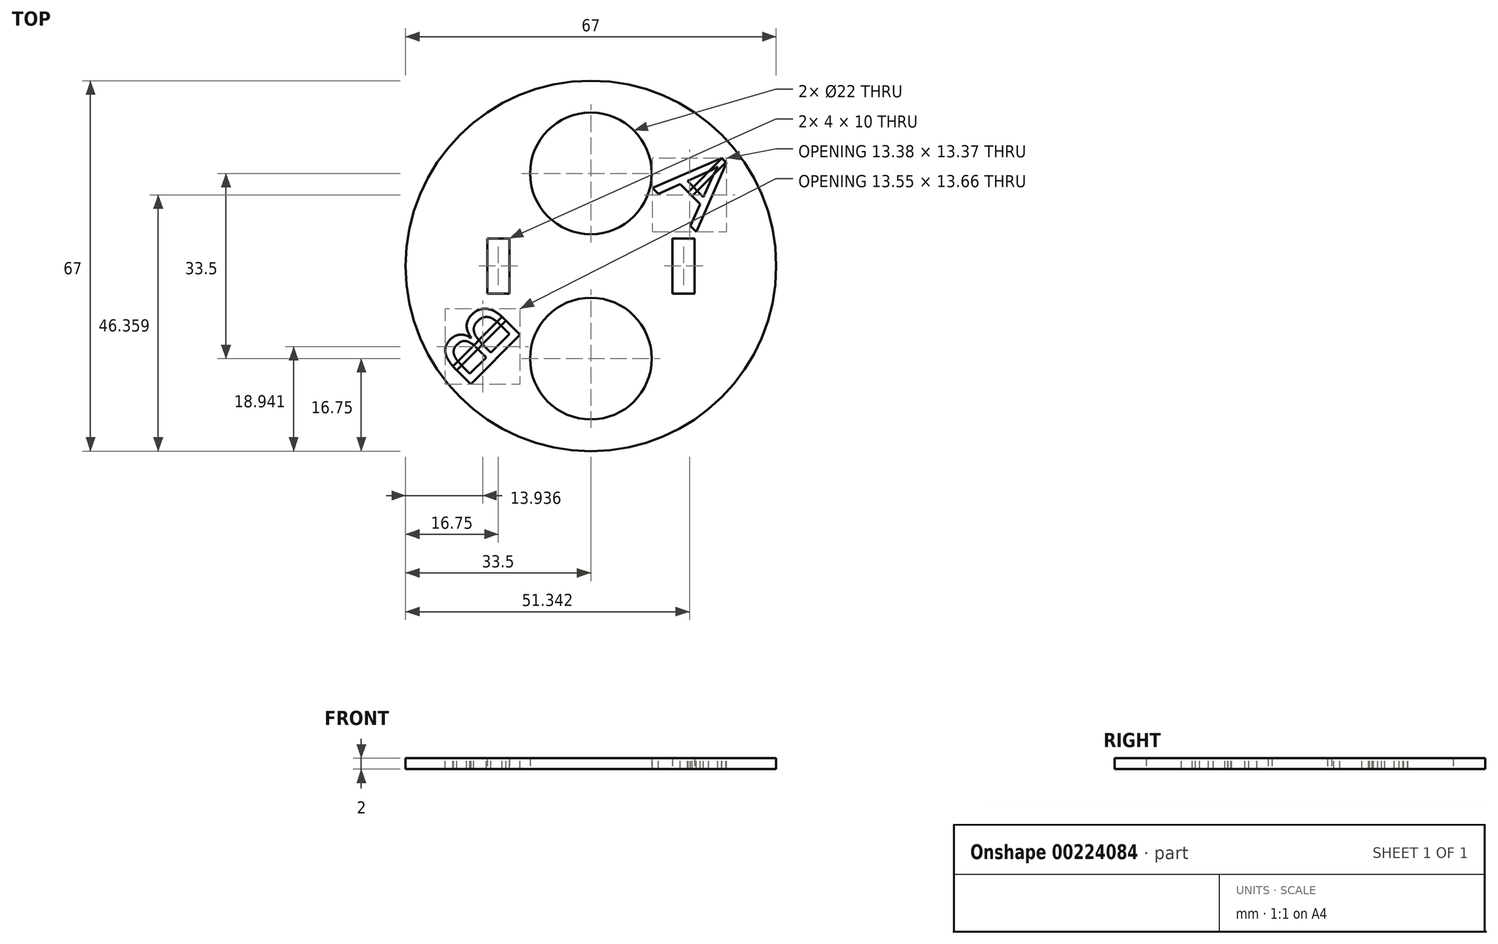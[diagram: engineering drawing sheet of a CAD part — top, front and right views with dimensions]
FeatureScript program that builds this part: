
annotation { "Feature Type Name" : "Feature", "Feature Type Description" : "" }
export const myFeature = defineFeature(function(context is Context, id is Id, definition is map)
    precondition{}
    {
        {
            assignVariable(context, id + "F0", {"name" : "thickness", "anyValue" : 2});
        }
        {
            var Q0;
            Q0=qCreatedBy(makeId("Top.planeOp"),FACE);
            var sketch = newSketch(context, id + "F1", { "sketchPlane" : qUnion([Q0])});
            skCircle(sketch, "E0", {"center": v(0, 0) * mm, "radius": 33.5 * mm});
            skLineSegment(sketch, "E1", {"start": v(0, 41.8) * mm, "end": v(0, -44.03) * mm});
            skLineSegment(sketch, "E2", {"start": v(41.2, 0) * mm, "end": v(-39.2, 0) * mm});
            skLineSegment(sketch, "E3", {"start": v(0, 0) * mm, "end": v(0, 33.5) * mm});
            skLineSegment(sketch, "E4", {"start": v(0, 33.5) * mm, "end": v(0, 16.75) * mm});
            skLineSegment(sketch, "E5", {"start": v(0, 0) * mm, "end": v(0, -16.75) * mm});
            skLineSegment(sketch, "E6", {"start": v(0, 0) * mm, "end": v(-16.75, 0) * mm});
            skLineSegment(sketch, "E7", {"start": v(0, 0) * mm, "end": v(16.75, 0) * mm});
            skCircle(sketch, "E8", {"center": v(0, 16.75) * mm, "radius": 11 * mm});
            skCircle(sketch, "E9", {"center": v(0, -16.75) * mm, "radius": 11 * mm});
            skLineSegment(sketch, "E10.bottom", {"start": v(-18.75, 5) * mm, "end": v(-14.75, 5) * mm});
            skLineSegment(sketch, "E10.top", {"start": v(-18.75, -5) * mm, "end": v(-14.75, -5) * mm});
            skLineSegment(sketch, "E10.left", {"start": v(-18.75, 5) * mm, "end": v(-18.75, -5) * mm});
            skLineSegment(sketch, "E10.right", {"start": v(-14.75, 5) * mm, "end": v(-14.75, -5) * mm});
            skPoint(sketch, "E10.middle", {"position": v(-16.75, 0) * mm});
            skLineSegment(sketch, "E11.bottom", {"start": v(14.75, 5) * mm, "end": v(18.75, 5) * mm});
            skLineSegment(sketch, "E11.top", {"start": v(14.75, -5) * mm, "end": v(18.75, -5) * mm});
            skLineSegment(sketch, "E11.left", {"start": v(14.75, 5) * mm, "end": v(14.75, -5) * mm});
            skLineSegment(sketch, "E11.right", {"start": v(18.75, 5) * mm, "end": v(18.75, -5) * mm});
            skPoint(sketch, "E11.middle", {"position": v(16.75, 0) * mm});
            skSolve(sketch);
        }
        {
            var Q0;
            {var subQ6=sQuery(id+"F1.wireOp",EDGE,"E2");var subQ9=sQuery(id+"F1.wireOp",EDGE,"E0");var subQ10=makeQuery(id+"F1.imprint","INTERSECT",VERTEX,{"disambiguationData":[OD(1.0)],"derivedFrom":[subQ9,subQ6]});Q0=makeQuery(id+"F1.imprint","IMPRINT",FACE,{"disambiguationData":[TD([[makeQuery(id+"F1.imprint","IMPRINT",EDGE,{"disambiguationData":[TD([[subQ10,-1.0]])],"derivedFrom":subQ9}),1.0]])]});}
            var Q1;
            {var subQ0=sQuery(id+"F1.wireOp",EDGE,"E4");var subQ1=sQuery(id+"F1.wireOp",EDGE,"E0");var subQ2=makeQuery(id+"F1.imprint","INTERSECT",VERTEX,{"derivedFrom":[subQ1,subQ0]});Q1=makeQuery(id+"F1.imprint","IMPRINT",FACE,{"disambiguationData":[TD([[makeQuery(id+"F1.imprint","IMPRINT",EDGE,{"disambiguationData":[TD([[subQ2,-1.0]])],"derivedFrom":subQ1}),1.0]])]});}
            var Q2;
            {var subQ0=sQuery(id+"F1.wireOp",EDGE,"E4");var subQ1=sQuery(id+"F1.wireOp",EDGE,"E0");var subQ2=makeQuery(id+"F1.imprint","INTERSECT",VERTEX,{"derivedFrom":[subQ1,subQ0]});Q2=makeQuery(id+"F1.imprint","IMPRINT",FACE,{"disambiguationData":[TD([[makeQuery(id+"F1.imprint","IMPRINT",EDGE,{"disambiguationData":[TD([[subQ2,1.0]])],"derivedFrom":subQ1}),1.0]])]});}
            var Q3;
            {var subQ5=sQuery(id+"F1.wireOp",EDGE,"E2");var subQ6=sQuery(id+"F1.wireOp",EDGE,"E0");var subQ7=makeQuery(id+"F1.imprint","INTERSECT",VERTEX,{"disambiguationData":[OD(0.0)],"derivedFrom":[subQ6,subQ5]});Q3=makeQuery(id+"F1.imprint","IMPRINT",FACE,{"disambiguationData":[TD([[makeQuery(id+"F1.imprint","IMPRINT",EDGE,{"disambiguationData":[TD([[subQ7,1.0]])],"derivedFrom":subQ6}),1.0]])]});}
            extrude(context, id + "F2", {"entities" : qUnion([Q0, Q1, Q2, Q3]), "depth" : (getVariable(context, 'thickness')) * mm});
        }
        {
            var Q0;
            Q0=makeQuery(id+"F2.opExtrude","CAP_FACE",FACE,{"disambiguationData":[OSD([sQuery(id+"F1.wireOp",EDGE,"E0"),sQuery(id+"F1.wireOp",EDGE,"E8"),sQuery(id+"F1.wireOp",EDGE,"E9"),sQuery(id+"F1.wireOp",EDGE,"E10.bottom"),sQuery(id+"F1.wireOp",EDGE,"E10.top"),sQuery(id+"F1.wireOp",EDGE,"E10.left"),sQuery(id+"F1.wireOp",EDGE,"E10.right"),sQuery(id+"F1.wireOp",EDGE,"E11.bottom"),sQuery(id+"F1.wireOp",EDGE,"E11.top"),sQuery(id+"F1.wireOp",EDGE,"E11.left"),sQuery(id+"F1.wireOp",EDGE,"E11.right")])],"isStart":false});
            var sketch = newSketch(context, id + "F3", { "sketchPlane" : qUnion([Q0])});
            skText(sketch, "E12", { "text": "A", "fontName": "OpenSans-Regular.ttf"});
            skText(sketch, "E13", { "text": "B", "fontName": "OpenSans-Regular.ttf"});
            skLineSegment(sketch, "E14", {"start": v(23.02, 17.94) * mm, "end": v(22.98, 17.9) * mm});
            skLineSegment(sketch, "E15", {"start": v(23.34, 17.55) * mm, "end": v(17.35, 11.56) * mm});
            const initialGuessF3  = {"E12": [0.01115, 0.0141, 0.7071, -0.7071, 0.01275], "E13": [-0.01156, -0.01368, -0.7071, 0.7071, 0.01275]};
            skSetInitialGuess(sketch, initialGuessF3);
            skSolve(sketch);
        }
        {
            var Q0;
            Q0=makeQuery(id+"F3.imprint","IMPRINT",FACE,{"disambiguationData":[TD([[makeQuery(id+"F3.imprint","IMPRINT",EDGE,{"derivedFrom":sQuery(id+"F3.wireOp",EDGE,"E13.sketch_text.stroke-0")}),-1.0]])]});
            var Q1;
            {var subQ1=sQuery(id+"F3.wireOp",EDGE,"E12.sketch_text.stroke-0");Q1=makeQuery(id+"F3.imprint","IMPRINT",FACE,{"disambiguationData":[TD([[makeQuery(id+"F3.imprint","IMPRINT",EDGE,{"derivedFrom":subQ1}),-1.0]])]});}
            extrude(context, id + "F4", {"entities" : qUnion([Q0, Q1]), "operationType" : NewBodyOperationType.REMOVE, "oppositeDirection" : true, "depth" : 25 * mm});
        }
        {
            var Q0;
            {var subQ0=sQuery(id+"F1.wireOp",EDGE,"E11.left");var subQ1=sQuery(id+"F1.wireOp",EDGE,"E0");var subQ2=sQuery(id+"F1.wireOp",EDGE,"E8");var subQ3=sQuery(id+"F1.wireOp",EDGE,"E11.right");var subQ4=sQuery(id+"F1.wireOp",EDGE,"E10.bottom");var subQ5=sQuery(id+"F1.wireOp",EDGE,"E9");var subQ6=sQuery(id+"F1.wireOp",EDGE,"E11.top");var subQ7=sQuery(id+"F1.wireOp",EDGE,"E10.left");var subQ8=sQuery(id+"F1.wireOp",EDGE,"E10.top");var subQ9=sQuery(id+"F1.wireOp",EDGE,"E10.right");var subQ10=sQuery(id+"F1.wireOp",EDGE,"E11.bottom");Q0=makeQuery(id+"F4.boolean.opBoolean","SPLIT",FACE,{"disambiguationData":[TD([makeQuery(id+"F2.opExtrude","SWEPT_FACE",FACE,{"disambiguationData":[OSD([subQ1])]})])],"derivedFrom":makeQuery(id+"F2.opExtrude","CAP_FACE",FACE,{"disambiguationData":[OSD([subQ1,subQ2,subQ5,subQ4,subQ8,subQ7,subQ9,subQ10,subQ6,subQ0,subQ3])],"isStart":false})});}
            var sketch = newSketch(context, id + "F5", { "sketchPlane" : qUnion([Q0])});
            skLineSegment(sketch, "E16", {"start": v(25.12, 20.18) * mm, "end": v(25.47, 19.82) * mm});
            skLineSegment(sketch, "E17", {"start": v(25.47, 19.82) * mm, "end": v(16.85, 11.2) * mm});
            skLineSegment(sketch, "E18", {"start": v(16.85, 11.2) * mm, "end": v(16.14, 11.91) * mm});
            skLineSegment(sketch, "E19", {"start": v(16.14, 11.91) * mm, "end": v(24.76, 20.53) * mm});
            skLineSegment(sketch, "E20", {"start": v(25.12, 20.18) * mm, "end": v(24.76, 20.53) * mm});
            skPoint(sketch, "E21.start.orphan", {"position": v(25.12, 20.89) * mm});
            skPoint(sketch, "E22.start.orphan", {"position": v(25.47, 20.53) * mm});
            skPoint(sketch, "E23.start.orphan", {"position": v(17.93, 13) * mm});
            skLineSegment(sketch, "E24", {"start": v(-25.35, -19.22) * mm, "end": v(-25.7, -18.86) * mm});
            skLineSegment(sketch, "E25", {"start": v(-25.7, -18.86) * mm, "end": v(-15.47, -8.63) * mm});
            skLineSegment(sketch, "E26", {"start": v(-15.47, -8.63) * mm, "end": v(-14.76, -9.33) * mm});
            skLineSegment(sketch, "E27", {"start": v(-14.76, -9.33) * mm, "end": v(-25, -19.57) * mm});
            skLineSegment(sketch, "E28", {"start": v(-25.35, -19.22) * mm, "end": v(-25, -19.57) * mm});
            skPoint(sketch, "E29.start.orphan", {"position": v(-25.7, -20.28) * mm});
            skSolve(sketch);
        }
        {
            var Q0;
            {var subQ0=sQuery(id+"F5.wireOp",EDGE,"E17");var subQ1=makeQuery(id+"F4.boolean.opBoolean","COPY",EDGE,{"derivedFrom":makeQuery(id+"F4.opExtrude","CAP_EDGE",EDGE,{"disambiguationData":[OSD([sQuery(id+"F3.wireOp",EDGE,"E12.sketch_text.stroke-5")])],"isStart":true})});var subQ2=makeQuery(id+"F5.imprint","INTERSECT",VERTEX,{"derivedFrom":[subQ1,subQ0]});Q0=makeQuery(id+"F5.imprint","IMPRINT",FACE,{"disambiguationData":[TD([[makeQuery(id+"F5.imprint","IMPRINT",EDGE,{"disambiguationData":[TD([[subQ2,-1.0]])],"derivedFrom":subQ0}),-1.0]])]});}
            var Q1;
            {var subQ3=sQuery(id+"F5.wireOp",EDGE,"E25");var subQ5=makeQuery(id+"F4.boolean.opBoolean","COPY",EDGE,{"derivedFrom":makeQuery(id+"F4.opExtrude","CAP_EDGE",EDGE,{"disambiguationData":[OSD([sQuery(id+"F3.wireOp",EDGE,"E13.sketch_text.stroke-1")])],"isStart":true})});var subQ6=makeQuery(id+"F5.imprint","INTERSECT",VERTEX,{"derivedFrom":[subQ5,subQ3]});Q1=makeQuery(id+"F5.imprint","IMPRINT",FACE,{"disambiguationData":[TD([[makeQuery(id+"F5.imprint","IMPRINT",EDGE,{"disambiguationData":[TD([[subQ6,-1.0]])],"derivedFrom":subQ3}),-1.0]])]});}
            extrude(context, id + "F6", {"entities" : qUnion([Q0, Q1]), "oppositeDirection" : true, "depth" : (getVariable(context, 'thickness')) * mm});
        }
    });
